# Revit family: Camera-Security-Panasonic-360-degree-Super_Dynamic-Dome-Network-SF438Series
name_source: partatom
category: Security Devices
revit_build: Autodesk Revit 2013 (Build: 20130531_2115(x64)
units: mm (PartAtom-declared; Revit-internal decimal feet)

## types (1)
- 3.1 Megapixels, RJ-45 Connector, WV-SF438
    Alarm Input Or Output Specification = ALARM IN 1, ALARM IN 2/ ALARM OUT, ALARM IN 3/ AUX OUT
    Angle Of View = 188
    Audio In = Yes
    Audio Out = Yes
    Auto Back Focus = Yes
    Communication Ports = 10Base-T / 100Base-TX, M12
    Date Last Modified = January, 23, 2015
    Day Or Night = Yes
    Default Elevation = 0 "
    Description = Security Camera, 360-degree, Super Dynamic, Dome, Network, SF438
    Diameter = 5.906 "
    Equipment Abbreviation = SC
    Family Version = 1.0.0
    Has POE = Yes
    Height = 1.732 "
    IP Or Analog = IP
    Indoor Or Outdoor = Indoor
    Manufacturer = Panasonic
    Minimum Illumination = 2 lx
    Model = WV-SF438
    Model Disclaimer = Contact Panasonic for more information
    Mounting Positions = Surface Mount
    Operational Humidity = 90% or less (without condensation)
    Operational Temperature = 14°F - 122°F
    Panning Range = -
    Part Description = Security Camera, 360-degree, Super Dynamic, Dome, Network, SF438
    Part Number = WV-SF438
    Power Active = 6.5 W
    Product Documentation Link = http://ssbu-t.psn-web.net
    Product Material = Paint - Panasonic - Sail White
    Product Page URL = http://security.panasonic.com
    Provide Feedback = https://www.surveymonkey.com
    Regulatory Compliance = UL 60950-1, FCC Part15 Class A, C-UL CAN/CSA C22.2 No.60950-1, ICES 003 Class A
    Storage Temperature = 14°F - 122°F
    Tilting Range = -
    URL = http://security.panasonic.com
    Vandal Resistant = No
    Voltage DC = 12 V
    Weight = 1.02 lb
    Wide Dynamic Range (Super Dynamic) = Yes
    z Base Height = 1.732 "
    z Base Radius = 2.953 "
    z Camera Height = 3.625 "
    z Dome Material = Glass - Panasonic - Smoked
    z Dome Radius = 0.433 "
    z Mount Height = 0.039 "
    z Type = 5

## geometry (parser evidence)
native form markers: Extrusion x1, Sweep x3
no freeform markers — native parametric forms only
